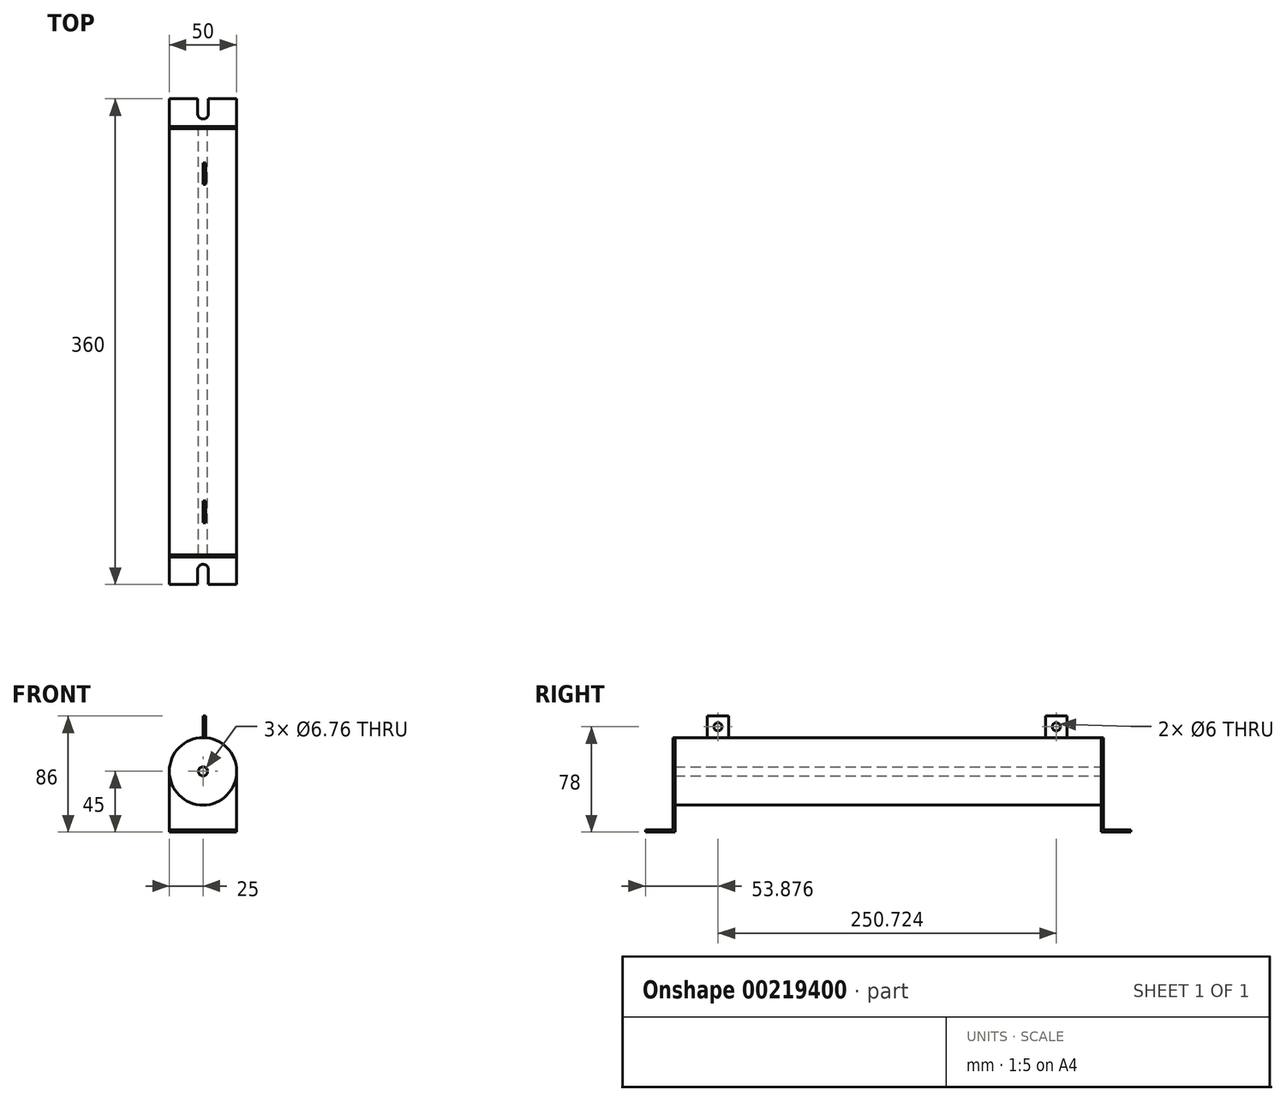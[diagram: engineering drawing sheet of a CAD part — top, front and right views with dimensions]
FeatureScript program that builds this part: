
annotation { "Feature Type Name" : "Feature", "Feature Type Description" : "" }
export const myFeature = defineFeature(function(context is Context, id is Id, definition is map)
    precondition{}
    {
        {
            var Q0;
            Q0=qCreatedBy(makeId("Front.planeOp"),FACE);
            var sketch = newSketch(context, id + "F0", { "sketchPlane" : qUnion([Q0])});
            skCircle(sketch, "E0", {"center": v(0, 0) * mm, "radius": 25 * mm});
            skSolve(sketch);
        }
        {
            var Q0;
            Q0=qSketchRegion(id+"F0",true);
            extrude(context, id + "F1", {"entities" : qUnion([Q0]), "oppositeDirection" : true, "depth" : 316 * mm});
        }
        {
            var Q0;
            Q0=qCreatedBy(makeId("Front.planeOp"),FACE);
            var sketch = newSketch(context, id + "F2", { "sketchPlane" : qUnion([Q0])});
            skCircle(sketch, "E1", {"center": v(0, 0) * mm, "radius": 25 * mm});
            skLineSegment(sketch, "E2.bottom", {"start": v(-25, 0) * mm, "end": v(25, 0) * mm});
            skLineSegment(sketch, "E2.top", {"start": v(-25, -45) * mm, "end": v(25, -45) * mm});
            skLineSegment(sketch, "E2.left", {"start": v(-25, 0) * mm, "end": v(-25, -45) * mm});
            skLineSegment(sketch, "E2.right", {"start": v(25, 0) * mm, "end": v(25, -45) * mm});
            skSolve(sketch);
        }
        {
            var Q0;
            Q0=qSketchRegion(id+"F2",true);
            extrude(context, id + "F3", {"entities" : qUnion([Q0]), "depth" : 1.52 * mm});
        }
        {
            var Q0;
            Q0=makeQuery(id+"F3.opExtrude","SWEPT_FACE",FACE,{"disambiguationData":[OSD([sQuery(id+"F2.wireOp",EDGE,"E2.top")])]});
            var sketch = newSketch(context, id + "F4", { "sketchPlane" : qUnion([Q0])});
            skLineSegment(sketch, "E3.bottom", {"start": v(-25, 0) * mm, "end": v(25, 0) * mm});
            skLineSegment(sketch, "E3.top", {"start": v(-25, 22) * mm, "end": v(25, 22) * mm});
            skLineSegment(sketch, "E3.left", {"start": v(-25, 0) * mm, "end": v(-25, 22) * mm});
            skLineSegment(sketch, "E3.right", {"start": v(25, 0) * mm, "end": v(25, 22) * mm});
            skSolve(sketch);
        }
        {
            var Q0;
            Q0=qSketchRegion(id+"F4",true);
            extrude(context, id + "F5", {"entities" : qUnion([Q0]), "operationType" : NewBodyOperationType.ADD, "oppositeDirection" : true, "depth" : 1.52 * mm});
        }
        {
            var Q0;
            Q0=makeQuery(id+"F5.boolean.opBoolean","MERGE",FACE,{"derivedFrom":[makeQuery(id+"F3.opExtrude","SWEPT_FACE",FACE,{"disambiguationData":[OSD([sQuery(id+"F2.wireOp",EDGE,"E2.top")])]}),makeQuery(id+"F5.opExtrude","CAP_FACE",FACE,{"disambiguationData":[OSD([sQuery(id+"F4.wireOp",EDGE,"E3.bottom"),sQuery(id+"F4.wireOp",EDGE,"E3.top"),sQuery(id+"F4.wireOp",EDGE,"E3.left"),sQuery(id+"F4.wireOp",EDGE,"E3.right")])],"isStart":true})]});
            var sketch = newSketch(context, id + "F6", { "sketchPlane" : qUnion([Q0])});
            skCircle(sketch, "E4", {"center": v(0, 11) * mm, "radius": 4 * mm});
            skPoint(sketch, "E4.centerSnap0", {"position": v(-25, 11) * mm});
            skLineSegment(sketch, "E5.bottom", {"start": v(-4, 22) * mm, "end": v(4, 22) * mm});
            skLineSegment(sketch, "E5.top", {"start": v(-4, 11) * mm, "end": v(4, 11) * mm});
            skLineSegment(sketch, "E5.left", {"start": v(-4, 22) * mm, "end": v(-4, 11) * mm});
            skLineSegment(sketch, "E5.right", {"start": v(4, 22) * mm, "end": v(4, 11) * mm});
            skSolve(sketch);
        }
        {
            var Q0;
            Q0=qSketchRegion(id+"F6",true);
            extrude(context, id + "F7", {"entities" : qUnion([Q0]), "operationType" : NewBodyOperationType.REMOVE, "oppositeDirection" : true, "depth" : 1.52 * mm});
        }
        {
            var Q0;
            Q0=makeQuery(id+"F1.opExtrude","CAP_FACE",FACE,{"disambiguationData":[OSD([sQuery(id+"F0.wireOp",EDGE,"E0")])],"isStart":false});
            var sketch = newSketch(context, id + "F8", { "sketchPlane" : qUnion([Q0])});
            skCircle(sketch, "E6", {"center": v(0, 0) * mm, "radius": 25 * mm});
            skLineSegment(sketch, "E7.bottom", {"start": v(-25, 0) * mm, "end": v(25, 0) * mm});
            skLineSegment(sketch, "E7.top", {"start": v(-25, -45) * mm, "end": v(25, -45) * mm});
            skLineSegment(sketch, "E7.left", {"start": v(-25, 0) * mm, "end": v(-25, -45) * mm});
            skLineSegment(sketch, "E7.right", {"start": v(25, 0) * mm, "end": v(25, -45) * mm});
            skSolve(sketch);
        }
        {
            var Q0;
            Q0=qSketchRegion(id+"F8",true);
            extrude(context, id + "F9", {"entities" : qUnion([Q0]), "depth" : 1.52 * mm});
        }
        {
            var Q0;
            Q0=makeQuery(id+"F9.opExtrude","SWEPT_FACE",FACE,{"disambiguationData":[OSD([sQuery(id+"F8.wireOp",EDGE,"E7.top")])]});
            var sketch = newSketch(context, id + "F10", { "sketchPlane" : qUnion([Q0])});
            skLineSegment(sketch, "E8.bottom", {"start": v(-25, -316) * mm, "end": v(25, -316) * mm});
            skLineSegment(sketch, "E8.top", {"start": v(-25, -338) * mm, "end": v(25, -338) * mm});
            skLineSegment(sketch, "E8.left", {"start": v(-25, -316) * mm, "end": v(-25, -338) * mm});
            skLineSegment(sketch, "E8.right", {"start": v(25, -316) * mm, "end": v(25, -338) * mm});
            skSolve(sketch);
        }
        {
            var Q0;
            {var subQ0=sQuery(id+"F10.wireOp",EDGE,"E8.top");Q0=makeQuery(id+"F10.imprint","IMPRINT",FACE,{"disambiguationData":[TD([[makeQuery(id+"F10.imprint","IMPRINT",EDGE,{"derivedFrom":subQ0}),1.0]])]});}
            extrude(context, id + "F11", {"entities" : qUnion([Q0]), "operationType" : NewBodyOperationType.ADD, "oppositeDirection" : true, "depth" : 1.52 * mm});
        }
        {
            var Q0;
            {var subQ0=sQuery(id+"F8.wireOp",EDGE,"E7.top");Q0=makeQuery(id+"F11.boolean.opBoolean","MERGE",FACE,{"derivedFrom":[makeQuery(id+"F9.opExtrude","SWEPT_FACE",FACE,{"disambiguationData":[OSD([subQ0])]}),makeQuery(id+"F11.opExtrude","CAP_FACE",FACE,{"disambiguationData":[OSD([subQ0,sQuery(id+"F10.wireOp",EDGE,"E8.top"),sQuery(id+"F10.wireOp",EDGE,"E8.left"),sQuery(id+"F10.wireOp",EDGE,"E8.right")])],"isStart":true})]});}
            var sketch = newSketch(context, id + "F12", { "sketchPlane" : qUnion([Q0])});
            skCircle(sketch, "E9", {"center": v(0, -327) * mm, "radius": 4 * mm});
            skPoint(sketch, "E9.centerSnap0", {"position": v(-25, -327) * mm});
            skPoint(sketch, "E9.centerSnap1", {"position": v(0, -316) * mm});
            skLineSegment(sketch, "E10.bottom", {"start": v(-4, -338) * mm, "end": v(4, -338) * mm});
            skLineSegment(sketch, "E10.top", {"start": v(-4, -327) * mm, "end": v(4, -327) * mm});
            skLineSegment(sketch, "E10.left", {"start": v(-4, -338) * mm, "end": v(-4, -327) * mm});
            skLineSegment(sketch, "E10.right", {"start": v(4, -338) * mm, "end": v(4, -327) * mm});
            skSolve(sketch);
        }
        {
            var Q0;
            Q0=qSketchRegion(id+"F12",true);
            extrude(context, id + "F13", {"entities" : qUnion([Q0]), "operationType" : NewBodyOperationType.REMOVE, "oppositeDirection" : true, "depth" : 1.52 * mm});
        }
        {
            var Q0;
            Q0=qCreatedBy(makeId("Right.planeOp"),FACE);
            var sketch = newSketch(context, id + "F14", { "sketchPlane" : qUnion([Q0])});
            skLineSegment(sketch, "E11.bottom", {"start": v(23.88, 41) * mm, "end": v(39.88, 41) * mm});
            skLineSegment(sketch, "E11.top", {"start": v(23.88, 25) * mm, "end": v(39.88, 25) * mm});
            skLineSegment(sketch, "E11.left", {"start": v(23.88, 41) * mm, "end": v(23.88, 25) * mm});
            skLineSegment(sketch, "E11.right", {"start": v(39.88, 41) * mm, "end": v(39.88, 25) * mm});
            skSolve(sketch);
        }
        {
            var Q0;
            Q0=makeQuery(id+"F14.imprint","IMPRINT",FACE,{"disambiguationData":[TD([[makeQuery(id+"F14.imprint","IMPRINT",EDGE,{"derivedFrom":sQuery(id+"F14.wireOp",EDGE,"E11.bottom")}),-1.0]])]});
            extrude(context, id + "F15", {"entities" : qUnion([Q0]), "depth" : 2 * mm});
        }
        {
            var Q0;
            Q0=makeQuery(id+"F15.opExtrude","CAP_FACE",FACE,{"disambiguationData":[OSD([sQuery(id+"F14.wireOp",EDGE,"E11.bottom"),sQuery(id+"F14.wireOp",EDGE,"E11.top"),sQuery(id+"F14.wireOp",EDGE,"E11.left"),sQuery(id+"F14.wireOp",EDGE,"E11.right")])],"isStart":false});
            var sketch = newSketch(context, id + "F16", { "sketchPlane" : qUnion([Q0])});
            skPoint(sketch, "E12", {"position": v(31.88, 33) * mm});
            skPoint(sketch, "E12.positionSnap0", {"position": v(23.88, 33) * mm});
            skPoint(sketch, "E12.positionSnap1", {"position": v(31.88, 41) * mm});
            skSolve(sketch);
        }
        {
            var Q0;
            Q0=sQuery(id+"F16.wireOp",VERTEX,"E12");
            var Q1;
            Q1=makeQuery(id+"F15.opExtrude","SWEPT_BODY",BODY,{"disambiguationData":[OSD([sQuery(id+"F14.wireOp",EDGE,"E11.bottom"),sQuery(id+"F14.wireOp",EDGE,"E11.top"),sQuery(id+"F14.wireOp",EDGE,"E11.left"),sQuery(id+"F14.wireOp",EDGE,"E11.right")])]});
            hole(context, id + "F17", {"style" : HoleStyle.SIMPLE, "endStyle" : HoleEndStyle.THROUGH, "holeDiameter" : 6 * mm, "locations" : qUnion([Q0]), "scope" : qUnion([Q1]), "isTappedThrough" : true, "startStyle" : HoleStartStyle.SKETCH});
        }
        {
            var Q0;
            Q0=qCreatedBy(makeId("Right.planeOp"),FACE);
            var sketch = newSketch(context, id + "F18", { "sketchPlane" : qUnion([Q0])});
            skLineSegment(sketch, "E13.bottom", {"start": v(290.6, 41) * mm, "end": v(274.6, 41) * mm});
            skLineSegment(sketch, "E13.top", {"start": v(290.6, 25) * mm, "end": v(274.6, 25) * mm});
            skLineSegment(sketch, "E13.left", {"start": v(290.6, 41) * mm, "end": v(290.6, 25) * mm});
            skLineSegment(sketch, "E13.right", {"start": v(274.6, 41) * mm, "end": v(274.6, 25) * mm});
            skSolve(sketch);
        }
        {
            var Q0;
            Q0=makeQuery(id+"F18.imprint","IMPRINT",FACE,{"disambiguationData":[TD([[makeQuery(id+"F18.imprint","IMPRINT",EDGE,{"derivedFrom":sQuery(id+"F18.wireOp",EDGE,"E13.bottom")}),1.0]])]});
            extrude(context, id + "F19", {"entities" : qUnion([Q0]), "depth" : 2 * mm});
        }
        {
            var Q0;
            Q0=makeQuery(id+"F19.opExtrude","CAP_FACE",FACE,{"disambiguationData":[OSD([sQuery(id+"F18.wireOp",EDGE,"E13.bottom"),sQuery(id+"F18.wireOp",EDGE,"E13.top"),sQuery(id+"F18.wireOp",EDGE,"E13.left"),sQuery(id+"F18.wireOp",EDGE,"E13.right")])],"isStart":true});
            var sketch = newSketch(context, id + "F20", { "sketchPlane" : qUnion([Q0])});
            skPoint(sketch, "E14", {"position": v(-282.6, 33) * mm});
            skPoint(sketch, "E14.positionSnap0", {"position": v(-290.6, 33) * mm});
            skPoint(sketch, "E14.positionSnap1", {"position": v(-282.6, 41) * mm});
            skSolve(sketch);
        }
        {
            var Q0;
            Q0=sQuery(id+"F20.wireOp",VERTEX,"E14");
            var Q1;
            Q1=makeQuery(id+"F19.opExtrude","SWEPT_BODY",BODY,{"disambiguationData":[OSD([sQuery(id+"F18.wireOp",EDGE,"E13.bottom"),sQuery(id+"F18.wireOp",EDGE,"E13.top"),sQuery(id+"F18.wireOp",EDGE,"E13.left"),sQuery(id+"F18.wireOp",EDGE,"E13.right")])]});
            hole(context, id + "F21", {"style" : HoleStyle.SIMPLE, "endStyle" : HoleEndStyle.THROUGH, "holeDiameter" : 6 * mm, "locations" : qUnion([Q0]), "scope" : qUnion([Q1]), "isTappedThrough" : true, "startStyle" : HoleStartStyle.SKETCH});
        }
        {
            var Q0;
            Q0=makeQuery(id+"F3.opExtrude","CAP_FACE",FACE,{"disambiguationData":[OSD([sQuery(id+"F2.wireOp",EDGE,"E1"),sQuery(id+"F2.wireOp",EDGE,"E2.top"),sQuery(id+"F2.wireOp",EDGE,"E2.left"),sQuery(id+"F2.wireOp",EDGE,"E2.right")])],"isStart":false});
            var sketch = newSketch(context, id + "F22", { "sketchPlane" : qUnion([Q0])});
            skPoint(sketch, "E15", {"position": v(0, 0) * mm});
            skSolve(sketch);
        }
        {
            var Q0;
            Q0=sQuery(id+"F22.wireOp",VERTEX,"E15");
            var Q1;
            Q1=makeQuery(id+"F3.opExtrude","SWEPT_BODY",BODY,{"disambiguationData":[OSD([sQuery(id+"F2.wireOp",EDGE,"E1"),sQuery(id+"F2.wireOp",EDGE,"E2.top"),sQuery(id+"F2.wireOp",EDGE,"E2.left"),sQuery(id+"F2.wireOp",EDGE,"E2.right")])]});
            var Q2;
            Q2=makeQuery(id+"F9.opExtrude","SWEPT_BODY",BODY,{"disambiguationData":[OSD([sQuery(id+"F8.wireOp",EDGE,"E6"),sQuery(id+"F8.wireOp",EDGE,"E7.top"),sQuery(id+"F8.wireOp",EDGE,"E7.left"),sQuery(id+"F8.wireOp",EDGE,"E7.right")])]});
            var Q3;
            Q3=makeQuery(id+"F1.opExtrude","SWEPT_BODY",BODY,{"disambiguationData":[OSD([sQuery(id+"F0.wireOp",EDGE,"E0")])]});
            hole(context, id + "F23", {"style" : HoleStyle.SIMPLE, "endStyle" : HoleEndStyle.THROUGH, "standardTappedOrClearance" : lookupTablePath({ "standard" : "ANSI", "fit" : "Normal (ASME)", "size" : "1/4", "type" : "Clearance" }), "standardBlindInLast" : lookupTablePath({ "fit" : "Free", "standard" : "ANSI", "size" : "1/4", "type" : "Clearance" }), "holeDiameter" : 6.76 * mm, "locations" : qUnion([Q0]), "scope" : qUnion([Q1, Q2, Q3]), "isTappedThrough" : true, "startStyle" : HoleStartStyle.SKETCH});
        }
    });
